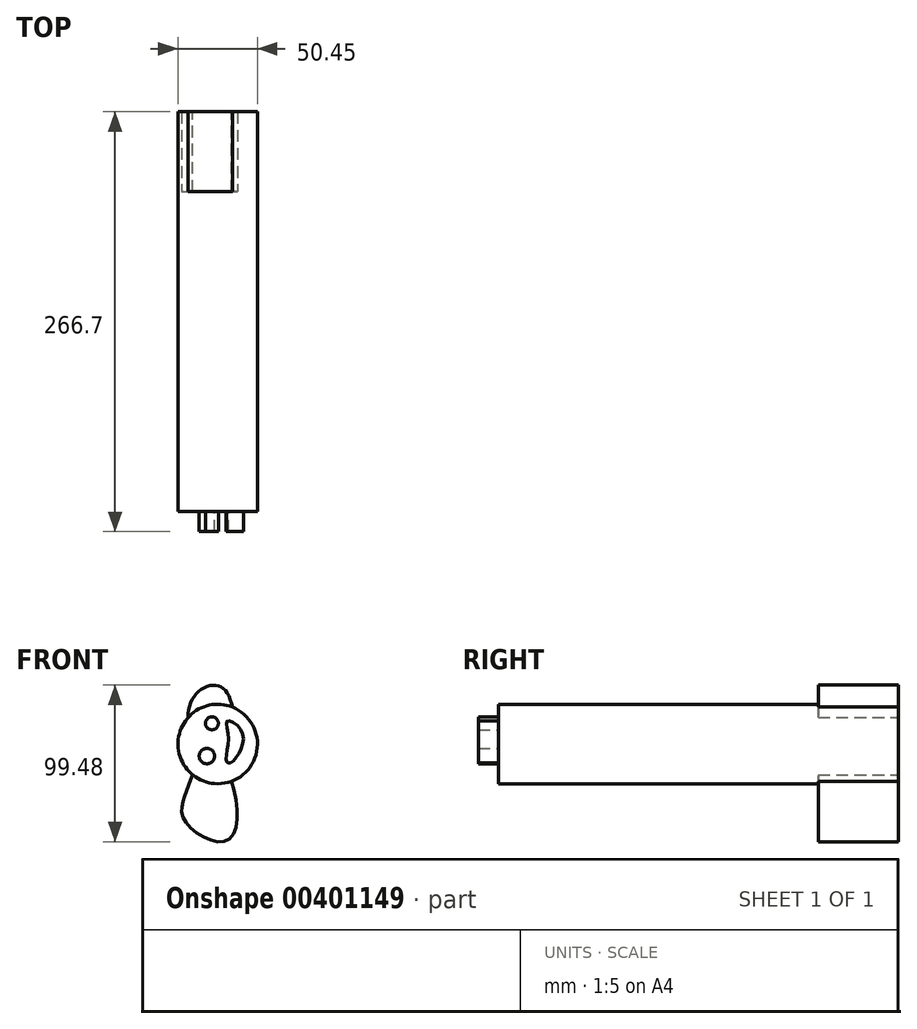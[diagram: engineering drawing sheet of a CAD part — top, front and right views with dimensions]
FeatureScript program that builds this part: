
annotation { "Feature Type Name" : "Feature", "Feature Type Description" : "" }
export const myFeature = defineFeature(function(context is Context, id is Id, definition is map)
    precondition{}
    {
        {
            var Q0;
            Q0=qCreatedBy(makeId("Front.planeOp"),FACE);
            var sketch = newSketch(context, id + "F0", { "sketchPlane" : qUnion([Q0])});
            skCircle(sketch, "E0", {"center": v(-37.84, 18.92) * mm, "radius": 25.23 * mm});
            skSolve(sketch);
        }
        {
            var Q0;
            Q0=makeQuery(id+"F0.imprint","IMPRINT",FACE,{"disambiguationData":[TD([[makeQuery(id+"F0.imprint","IMPRINT",EDGE,{"derivedFrom":sQuery(id+"F0.wireOp",EDGE,"E0")}),1.0]])]});
            extrude(context, id + "F1", {"entities" : qUnion([Q0]), "depth" : 254 * mm});
        }
        {
            var Q0;
            Q0=makeQuery(id+"F1.opExtrude","CAP_FACE",FACE,{"disambiguationData":[OSD([sQuery(id+"F0.wireOp",EDGE,"E0")])],"isStart":false});
            var sketch = newSketch(context, id + "F2", { "sketchPlane" : qUnion([Q0])});
            skCircle(sketch, "E1", {"center": v(-41.5, 32.08) * mm, "radius": 4.11 * mm});
            skCircle(sketch, "E2", {"center": v(-44.7, 11.26) * mm, "radius": 4.9 * mm});
            skFitSpline(sketch, "E3", {"points": [v(-30.96, 22.09) * mm, v(-31.78, 33.5) * mm, v(-23.15, 28.22) * mm, v(-23.78, 13.92) * mm, v(-30.45, 6.8) * mm, v(-32.55, 8.5) * mm, v(-30.96, 22.09) * mm]});
            skSolve(sketch);
        }
        {
            var Q0;
            Q0=makeQuery(id+"F2.imprint","IMPRINT",FACE,{"disambiguationData":[TD([[makeQuery(id+"F2.imprint","IMPRINT",EDGE,{"derivedFrom":sQuery(id+"F2.wireOp",EDGE,"E2")}),1.0]])]});
            var Q1;
            Q1=makeQuery(id+"F2.imprint","IMPRINT",FACE,{"disambiguationData":[TD([[makeQuery(id+"F2.imprint","IMPRINT",EDGE,{"derivedFrom":sQuery(id+"F2.wireOp",EDGE,"E1")}),1.0]])]});
            var Q2;
            Q2=makeQuery(id+"F2.imprint","IMPRINT",FACE,{"disambiguationData":[TD([[makeQuery(id+"F2.imprint","IMPRINT",EDGE,{"derivedFrom":sQuery(id+"F2.wireOp",EDGE,"E3")}),-1.0]])]});
            extrude(context, id + "F3", {"entities" : qUnion([Q0, Q1, Q2]), "operationType" : NewBodyOperationType.ADD, "depth" : 12.7 * mm});
        }
        {
            var Q0;
            Q0=qCreatedBy(makeId("Front.planeOp"),FACE);
            var sketch = newSketch(context, id + "F4", { "sketchPlane" : qUnion([Q0])});
            skFitSpline(sketch, "E4", {"points": [v(-45.12, 12.17) * mm, v(-55.32, 44.58) * mm, v(-35.1, 54.86) * mm, v(-30.62, 17.76) * mm, v(-45.12, 12.17) * mm]});
            skFitSpline(sketch, "E5", {"points": [v(-57.32, -10.18) * mm, v(-48.3, 7.1) * mm, v(-33.45, 3.68) * mm, v(-30.5, -41.47) * mm, v(-58.75, -29.83) * mm, v(-57.32, -10.18) * mm]});
            skSolve(sketch);
        }
        {
            var Q0;
            Q0=makeQuery(id+"F4.imprint","IMPRINT",FACE,{"disambiguationData":[TD([[makeQuery(id+"F4.imprint","IMPRINT",EDGE,{"derivedFrom":sQuery(id+"F4.wireOp",EDGE,"E4")}),-1.0]])]});
            var Q1;
            Q1=makeQuery(id+"F4.imprint","IMPRINT",FACE,{"disambiguationData":[TD([[makeQuery(id+"F4.imprint","IMPRINT",EDGE,{"derivedFrom":sQuery(id+"F4.wireOp",EDGE,"E5")}),-1.0]])]});
            extrude(context, id + "F5", {"entities" : qUnion([Q0, Q1]), "operationType" : NewBodyOperationType.ADD, "depth" : 50.8 * mm});
        }
    });
